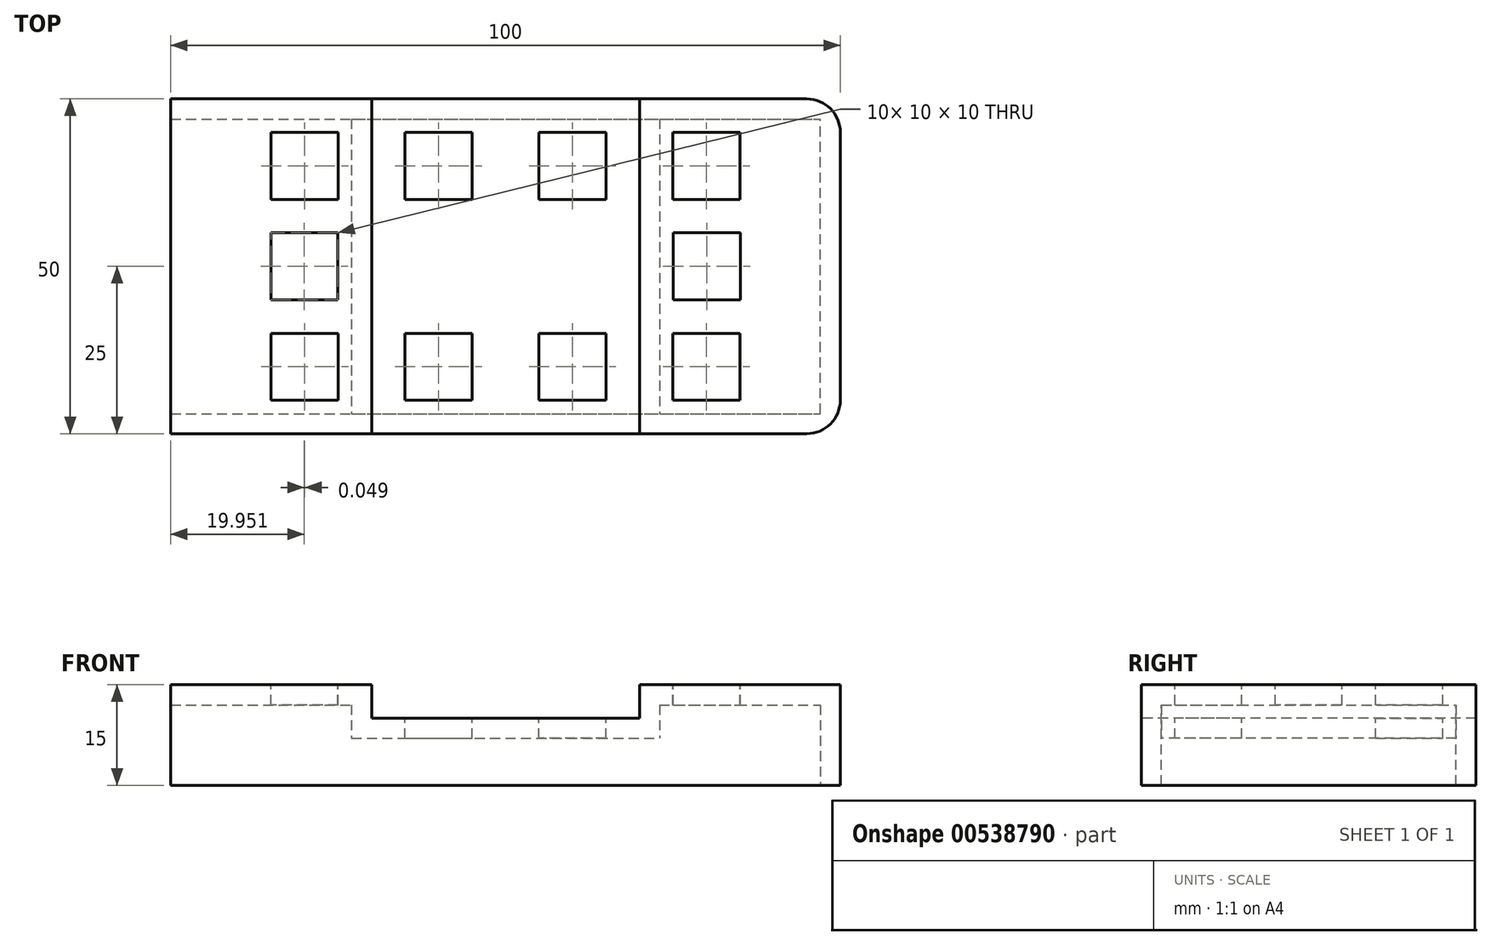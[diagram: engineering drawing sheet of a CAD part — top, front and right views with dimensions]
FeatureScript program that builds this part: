
annotation { "Feature Type Name" : "Feature", "Feature Type Description" : "" }
export const myFeature = defineFeature(function(context is Context, id is Id, definition is map)
    precondition{}
    {
        {
            assignVariable(context, id + "F0", {"name" : "C", "anyValue" : 3});
        }
        {
            var Q0;
            Q0=qCreatedBy(makeId("Top.planeOp"),FACE);
            var sketch = newSketch(context, id + "F1", { "sketchPlane" : qUnion([Q0])});
            skLineSegment(sketch, "E0.bottom", {"start": v(0, 0) * mm, "end": v(100, 0) * mm});
            skLineSegment(sketch, "E0.top", {"start": v(0, 50) * mm, "end": v(100, 50) * mm});
            skLineSegment(sketch, "E0.left", {"start": v(0, 0) * mm, "end": v(0, 50) * mm});
            skLineSegment(sketch, "E0.right", {"start": v(100, 0) * mm, "end": v(100, 50) * mm});
            skSolve(sketch);
        }
        {
            var Q0;
            Q0 = qSketchRegion(id + "F1", true);
            extrude(context, id + "F2", {"entities" : qUnion([Q0]), "depth" : 15 * mm, "offsetDistance" : 25 * mm});
        }
        {
            var Q0;
            Q0=qCreatedBy(makeId("Front.planeOp"),FACE);
            var sketch = newSketch(context, id + "F3", { "sketchPlane" : qUnion([Q0])});
            skLineSegment(sketch, "E1.bottom", {"start": v(30, 15) * mm, "end": v(70, 15) * mm});
            skLineSegment(sketch, "E1.top", {"start": v(30, 10) * mm, "end": v(70, 10) * mm});
            skLineSegment(sketch, "E1.left", {"start": v(30, 15) * mm, "end": v(30, 10) * mm});
            skLineSegment(sketch, "E1.right", {"start": v(70, 15) * mm, "end": v(70, 10) * mm});
            skSolve(sketch);
        }
        {
            var Q0;
            Q0 = qSketchRegion(id + "F3", true);
            extrude(context, id + "F4", {"entities" : qUnion([Q0]), "operationType" : NewBodyOperationType.REMOVE, "endBound" : BoundingType.UP_TO_NEXT, "oppositeDirection" : true, "depth" : 25 * mm, "offsetDistance" : 25 * mm});
        }
        {
            var Q0;
            Q0=makeQuery(id+"F2.opExtrude","CAP_FACE",FACE,{"disambiguationData":[OSD([sQuery(id+"F1.wireOp",EDGE,"E0.bottom"),sQuery(id+"F1.wireOp",EDGE,"E0.top"),sQuery(id+"F1.wireOp",EDGE,"E0.left"),sQuery(id+"F1.wireOp",EDGE,"E0.right")])],"isStart":true});
            shell(context, id + "F5", {"entities" : qUnion([Q0]), "thickness" : (getVariable(context, 'C')) * mm});
        }
        {
            var Q0;
            Q0=makeQuery(id+"F2.opExtrude","SWEPT_FACE",FACE,{"disambiguationData":[OSD([sQuery(id+"F1.wireOp",EDGE,"E0.left")])]});
            var sketch = newSketch(context, id + "F6", { "sketchPlane" : qUnion([Q0])});
            skLineSegment(sketch, "E2.bottom", {"start": v(-47, 0) * mm, "end": v(-3, 0) * mm});
            skLineSegment(sketch, "E2.top", {"start": v(-47, 12) * mm, "end": v(-3, 12) * mm});
            skLineSegment(sketch, "E2.left", {"start": v(-47, 0) * mm, "end": v(-47, 12) * mm});
            skLineSegment(sketch, "E2.right", {"start": v(-3, 0) * mm, "end": v(-3, 12) * mm});
            skSolve(sketch);
        }
        {
            var Q0;
            Q0 = qSketchRegion(id + "F6", true);
            extrude(context, id + "F7", {"entities" : qUnion([Q0]), "operationType" : NewBodyOperationType.REMOVE, "endBound" : BoundingType.UP_TO_NEXT, "oppositeDirection" : true, "depth" : 25 * mm, "offsetDistance" : 25 * mm});
        }
        {
            var Q0;
            Q0=qCreatedBy(makeId("Top.planeOp"),FACE);
            cPlane(context, id + "F8", {"entities" : qUnion([Q0]), "cplaneType" : CPlaneType.OFFSET, "offset" : 15 * mm, "width" : 150 * mm, "height" : 150 * mm});
        }
        {
            var Q0;
            Q0=qCreatedBy(id+"F8.planeOp",FACE);
            var sketch = newSketch(context, id + "F9", { "sketchPlane" : qUnion([Q0])});
            skLineSegment(sketch, "E3.bottom", {"start": v(75, 45) * mm, "end": v(85, 45) * mm});
            skLineSegment(sketch, "E3.top", {"start": v(75, 35) * mm, "end": v(85, 35) * mm});
            skLineSegment(sketch, "E3.left", {"start": v(75, 45) * mm, "end": v(75, 35) * mm});
            skLineSegment(sketch, "E3.right", {"start": v(85, 45) * mm, "end": v(85, 35) * mm});
            skLineSegment(sketch, "E4", {"start": v(-12.28, 25) * mm, "end": v(99.83, 25) * mm, "construction": true});
            skLineSegment(sketch, "E5.MirrorCS", {"start": v(75, 15) * mm, "end": v(85, 15) * mm});
            skLineSegment(sketch, "E6.MirrorCS", {"start": v(75, 5) * mm, "end": v(85, 5) * mm});
            skLineSegment(sketch, "E7.MirrorCS", {"start": v(75, 5) * mm, "end": v(75, 15) * mm});
            skLineSegment(sketch, "E8.MirrorCS", {"start": v(85, 5) * mm, "end": v(85, 15) * mm});
            skLineSegment(sketch, "E9.bottom", {"start": v(75.05, 30) * mm, "end": v(85.05, 30) * mm});
            skLineSegment(sketch, "E9.top", {"start": v(75.05, 20) * mm, "end": v(85.05, 20) * mm});
            skLineSegment(sketch, "E9.left", {"start": v(75.05, 30) * mm, "end": v(75.05, 20) * mm});
            skLineSegment(sketch, "E9.right", {"start": v(85.05, 30) * mm, "end": v(85.05, 20) * mm});
            skLineSegment(sketch, "E10", {"start": v(50, 58.24) * mm, "end": v(50, -15.59) * mm, "construction": true});
            skLineSegment(sketch, "E11.MirrorCS", {"start": v(25, 45) * mm, "end": v(25, 35) * mm});
            skLineSegment(sketch, "E12.MirrorCS", {"start": v(15, 45) * mm, "end": v(15, 35) * mm});
            skLineSegment(sketch, "E13.MirrorCS", {"start": v(25, 45) * mm, "end": v(15, 45) * mm});
            skLineSegment(sketch, "E14.MirrorCS", {"start": v(25, 35) * mm, "end": v(15, 35) * mm});
            skLineSegment(sketch, "E15.MirrorCS", {"start": v(24.95, 30) * mm, "end": v(14.95, 30) * mm});
            skLineSegment(sketch, "E16.MirrorCS", {"start": v(24.95, 30) * mm, "end": v(24.95, 20) * mm});
            skLineSegment(sketch, "E17.MirrorCS", {"start": v(14.95, 30) * mm, "end": v(14.95, 20) * mm});
            skLineSegment(sketch, "E18.MirrorCS", {"start": v(24.95, 20) * mm, "end": v(14.95, 20) * mm});
            skLineSegment(sketch, "E19.MirrorCS", {"start": v(25, 15) * mm, "end": v(15, 15) * mm});
            skLineSegment(sketch, "E20.MirrorCS", {"start": v(25, 5) * mm, "end": v(25, 15) * mm});
            skLineSegment(sketch, "E21.MirrorCS", {"start": v(25, 5) * mm, "end": v(15, 5) * mm});
            skLineSegment(sketch, "E22.MirrorCS", {"start": v(15, 5) * mm, "end": v(15, 15) * mm});
            skLineSegment(sketch, "E23.bottom", {"start": v(55, 45) * mm, "end": v(65, 45) * mm});
            skLineSegment(sketch, "E23.top", {"start": v(55, 35) * mm, "end": v(65, 35) * mm});
            skLineSegment(sketch, "E23.left", {"start": v(55, 45) * mm, "end": v(55, 35) * mm});
            skLineSegment(sketch, "E23.right", {"start": v(65, 45) * mm, "end": v(65, 35) * mm});
            skLineSegment(sketch, "E24.MirrorCS", {"start": v(55, 15) * mm, "end": v(65, 15) * mm});
            skLineSegment(sketch, "E25.MirrorCS", {"start": v(55, 5) * mm, "end": v(65, 5) * mm});
            skLineSegment(sketch, "E26.MirrorCS", {"start": v(55, 5) * mm, "end": v(55, 15) * mm});
            skLineSegment(sketch, "E27.MirrorCS", {"start": v(65, 5) * mm, "end": v(65, 15) * mm});
            skLineSegment(sketch, "E28.MirrorCS", {"start": v(45, 45) * mm, "end": v(45, 35) * mm});
            skLineSegment(sketch, "E29.MirrorCS", {"start": v(45, 35) * mm, "end": v(35, 35) * mm});
            skLineSegment(sketch, "E30.MirrorCS", {"start": v(45, 45) * mm, "end": v(35, 45) * mm});
            skLineSegment(sketch, "E31.MirrorCS", {"start": v(35, 45) * mm, "end": v(35, 35) * mm});
            skLineSegment(sketch, "E32.MirrorCS", {"start": v(45, 15) * mm, "end": v(35, 15) * mm});
            skLineSegment(sketch, "E33.MirrorCS", {"start": v(45, 5) * mm, "end": v(45, 15) * mm});
            skLineSegment(sketch, "E34.MirrorCS", {"start": v(45, 5) * mm, "end": v(35, 5) * mm});
            skLineSegment(sketch, "E35.MirrorCS", {"start": v(35, 5) * mm, "end": v(35, 15) * mm});
            skSolve(sketch);
        }
        {
            var Q0;
            Q0 = qSketchRegion(id + "F9", true);
            extrude(context, id + "F10", {"entities" : qUnion([Q0]), "operationType" : NewBodyOperationType.REMOVE, "endBound" : BoundingType.THROUGH_ALL, "oppositeDirection" : true, "depth" : 25 * mm, "offsetDistance" : 25 * mm});
        }
        {
            var Q0;
            Q0=makeQuery(id+"F2.opExtrude","SWEPT_EDGE",EDGE,{"disambiguationData":[OSD([sQuery(id+"F1.wireOp",EDGE,"E0.bottom"),sQuery(id+"F1.wireOp",EDGE,"E0.right")])]});
            var Q1;
            Q1=makeQuery(id+"F2.opExtrude","SWEPT_EDGE",EDGE,{"disambiguationData":[OSD([sQuery(id+"F1.wireOp",EDGE,"E0.top"),sQuery(id+"F1.wireOp",EDGE,"E0.right")])]});
            fillet(context, id + "F11", {"entities" : qUnion([Q0, Q1]), "radius" : 5 * mm, "tangentPropagation" : true, "allowEdgeOverflow" : false});
        }
    });
